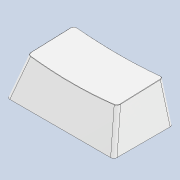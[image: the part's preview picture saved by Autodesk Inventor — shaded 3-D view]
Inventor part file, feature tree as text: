
AUTODESK INVENTOR PART (.ipt)
format: ipt  version: 2021 (Build 250183000, 183)  size: 226,304 bytes
history: native  units: in
note: dims shown in document units (in); Inventor stores cm internally (conversion verified against a paired STEP export)
features: chamfer x1
ambient origin geometry x8: Origin, YZ Plane, XZ Plane, XY Plane, X Axis, Y Axis, Z Axis, Center Point
bodies: Solid1 (feature_tree)
feature tree (1):
  chamfer  "Chamfer1"  [1 undecoded]
note: 1 required parameter value undecoded (feature->parameter linkage not recoverable at this tier; creation-order binding heuristic only, values carry confidence <= 0.55)
